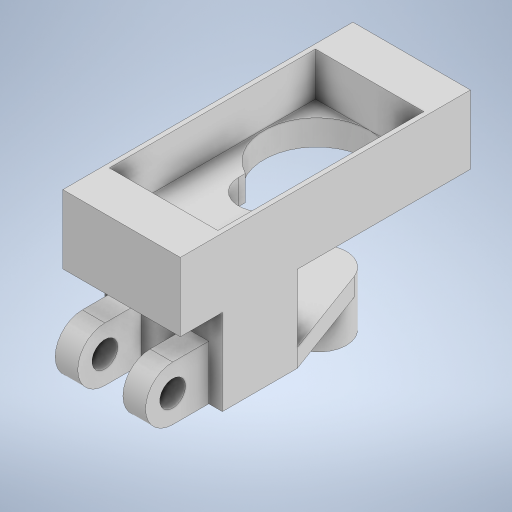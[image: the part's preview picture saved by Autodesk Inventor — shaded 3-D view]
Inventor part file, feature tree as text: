
AUTODESK INVENTOR PART (.ipt)
format: ipt  version: 2023 (Build 270158000, 158)  size: 342,016 bytes
history: native  units: mm
features: extrude x7, sketch x6
ambient origin geometry x8: Origin, YZ Plane, XZ Plane, XY Plane, X Axis, Y Axis, Z Axis, Center Point
bodies: Solid1 (feature_tree)
feature tree (13):
  sketch  "Sketch1"  dims[d0=22.8mm d1=12.0mm]
  extrude  "Extrusion1"  Depth=12.0mm
  extrude  "Extrusion3"  Depth=0.5mm
  extrude  "Extrusion8"  Depth=4.65mm
  extrude  "Extrusion9"  Depth=7.6mm TaperAngle=0.0deg
  extrude  "Extrusion10"  Depth=2.8mm
  extrude  "Extrusion11"  Depth=4.65mm
  extrude  "Extrusion12"  Depth=8.3mm
  sketch  "Sketch5"  dims[d5=4.65mm d6=0.5mm]
  sketch  "Sketch6"  dims[d7=0.5mm d8=4.65mm]
  sketch  "Sketch7"  dims[d9=2.8mm d10=0.0mm d13=7.6mm d14=0.0mm]
  sketch  "Sketch8"  dims[d42=11.7mm d43=2.8mm]
  sketch  "Sketch9"  dims[d44=2.75mm d45=4.65mm d46=8.3mm d47=7.5mm d48=0.0mm d49=5.6mm d50=6.05mm d51=2.0mm d52=0.0mm d53=5.6mm d54=6.05mm d55=4.0mm d56=0.0mm d58=2.5mm d59=2.5mm d60=6.0mm d61=6.0mm d62=2.5mm d63=2.5mm d64=7.0mm d65=0.0mm d66=2.85mm d67=3.0mm d68=0.0mm d69=0.0mm]
